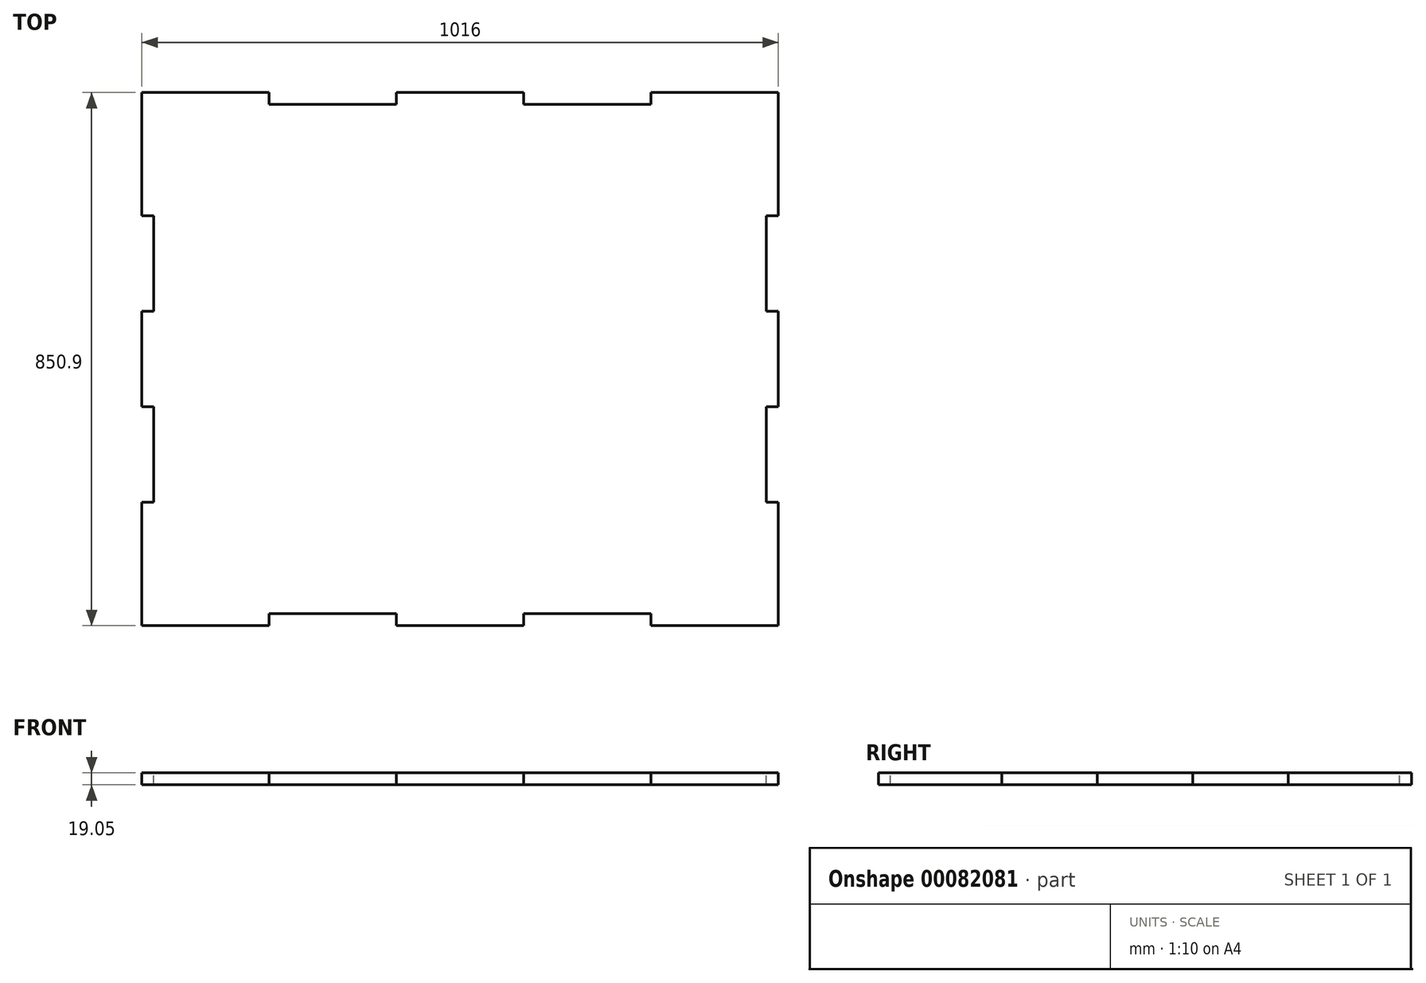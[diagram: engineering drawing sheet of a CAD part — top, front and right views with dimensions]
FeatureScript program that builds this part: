
annotation { "Feature Type Name" : "Feature", "Feature Type Description" : "" }
export const myFeature = defineFeature(function(context is Context, id is Id, definition is map)
    precondition{}
    {
        {
            var Q0;
            Q0=qCreatedBy(makeId("Top.planeOp"),FACE);
            var sketch = newSketch(context, id + "F0", { "sketchPlane" : qUnion([Q0])});
            skLineSegment(sketch, "E0.bottom", {"start": v(-612.36, 0) * mm, "end": v(403.64, 0) * mm});
            skLineSegment(sketch, "E0.top", {"start": v(-612.36, 838.2) * mm, "end": v(403.64, 838.2) * mm});
            skLineSegment(sketch, "E0.left", {"start": v(-612.36, 0) * mm, "end": v(-612.36, 838.2) * mm});
            skLineSegment(sketch, "E0.right", {"start": v(403.64, 0) * mm, "end": v(403.64, 838.2) * mm});
            skSolve(sketch);
        }
        {
            var Q0;
            Q0 = qSketchRegion(id + "F0", true);
            extrude(context, id + "F1", {"entities" : qUnion([Q0]), "depth" : 19.05 * mm});
        }
        {
            var Q0;
            Q0=makeQuery(id+"F1.opExtrude","CAP_FACE",FACE,{"disambiguationData":[OSD([sQuery(id+"F0.wireOp",EDGE,"E0.bottom"),sQuery(id+"F0.wireOp",EDGE,"E0.top"),sQuery(id+"F0.wireOp",EDGE,"E0.left"),sQuery(id+"F0.wireOp",EDGE,"E0.right")])],"isStart":false});
            var sketch = newSketch(context, id + "F2", { "sketchPlane" : qUnion([Q0])});
            skLineSegment(sketch, "E1", {"start": v(403.64, 190.5) * mm, "end": v(390.94, 190.5) * mm});
            skLineSegment(sketch, "E2", {"start": v(390.94, 190.5) * mm, "end": v(390.94, 342.9) * mm});
            skLineSegment(sketch, "E3", {"start": v(390.94, 342.9) * mm, "end": v(403.64, 342.9) * mm});
            skLineSegment(sketch, "E4", {"start": v(403.64, 495.3) * mm, "end": v(384.6, 495.3) * mm});
            skLineSegment(sketch, "E5", {"start": v(384.6, 495.3) * mm, "end": v(384.6, 647.7) * mm});
            skLineSegment(sketch, "E6", {"start": v(384.6, 647.7) * mm, "end": v(403.64, 647.7) * mm});
            skLineSegment(sketch, "E7.top", {"start": v(384.6, 495.3) * mm, "end": v(403.64, 495.3) * mm});
            skLineSegment(sketch, "E7.left", {"start": v(384.6, 647.7) * mm, "end": v(384.6, 495.3) * mm});
            skLineSegment(sketch, "E7.right", {"start": v(403.64, 647.7) * mm, "end": v(403.64, 495.3) * mm});
            skLineSegment(sketch, "E8.top", {"start": v(390.94, 190.5) * mm, "end": v(403.64, 190.5) * mm});
            skLineSegment(sketch, "E8.left", {"start": v(390.94, 342.9) * mm, "end": v(390.94, 190.5) * mm});
            skLineSegment(sketch, "E8.right", {"start": v(403.64, 342.9) * mm, "end": v(403.64, 190.5) * mm});
            skLineSegment(sketch, "E9.MirrorCS", {"start": v(-599.66, 342.9) * mm, "end": v(-612.36, 342.9) * mm});
            skLineSegment(sketch, "E10.MirrorCS", {"start": v(-599.66, 190.5) * mm, "end": v(-612.36, 190.5) * mm});
            skLineSegment(sketch, "E11.MirrorCS", {"start": v(-612.36, 190.5) * mm, "end": v(-599.66, 190.5) * mm});
            skLineSegment(sketch, "E12.MirrorCS", {"start": v(-599.66, 342.9) * mm, "end": v(-599.66, 190.5) * mm});
            skLineSegment(sketch, "E13.MirrorCS", {"start": v(-599.66, 190.5) * mm, "end": v(-599.66, 342.9) * mm});
            skLineSegment(sketch, "E14.MirrorCS", {"start": v(-612.36, 342.9) * mm, "end": v(-612.36, 190.5) * mm});
            skLineSegment(sketch, "E15.MirrorCS", {"start": v(-612.36, 495.3) * mm, "end": v(-599.66, 495.3) * mm});
            skLineSegment(sketch, "E16.MirrorCS", {"start": v(-599.66, 647.7) * mm, "end": v(-612.36, 647.7) * mm});
            skLineSegment(sketch, "E17.MirrorCS", {"start": v(-599.66, 495.3) * mm, "end": v(-612.36, 495.3) * mm});
            skLineSegment(sketch, "E18.MirrorCS", {"start": v(-599.66, 495.3) * mm, "end": v(-599.66, 647.7) * mm});
            skLineSegment(sketch, "E19.MirrorCS", {"start": v(-612.36, 647.7) * mm, "end": v(-612.36, 495.3) * mm});
            skLineSegment(sketch, "E20.MirrorCS", {"start": v(-599.66, 647.7) * mm, "end": v(-599.66, 495.3) * mm});
            skLineSegment(sketch, "E21", {"start": v(-409.16, 0) * mm, "end": v(-409.16, 19.05) * mm});
            skLineSegment(sketch, "E22", {"start": v(-409.16, 19.05) * mm, "end": v(-205.96, 19.05) * mm});
            skLineSegment(sketch, "E23", {"start": v(-205.96, 19.05) * mm, "end": v(-205.96, 0) * mm});
            skLineSegment(sketch, "E24", {"start": v(-2.76, 0) * mm, "end": v(-2.76, 19.05) * mm});
            skLineSegment(sketch, "E25", {"start": v(-2.76, 19.05) * mm, "end": v(200.44, 19.05) * mm});
            skLineSegment(sketch, "E26", {"start": v(200.44, 19.05) * mm, "end": v(200.44, 0) * mm});
            skLineSegment(sketch, "E27", {"start": v(-409.16, 0) * mm, "end": v(-205.96, 0) * mm});
            skLineSegment(sketch, "E28", {"start": v(403.64, 419.1) * mm, "end": v(-612.36, 419.1) * mm});
            skLineSegment(sketch, "E29.MirrorCS", {"start": v(200.44, 819.15) * mm, "end": v(200.44, 838.2) * mm});
            skLineSegment(sketch, "E30.MirrorCS", {"start": v(-409.16, 838.2) * mm, "end": v(-409.16, 819.15) * mm});
            skLineSegment(sketch, "E31.MirrorCS", {"start": v(-205.96, 819.15) * mm, "end": v(-205.96, 838.2) * mm});
            skLineSegment(sketch, "E32.MirrorCS", {"start": v(-2.76, 819.15) * mm, "end": v(200.44, 819.15) * mm});
            skLineSegment(sketch, "E33.MirrorCS", {"start": v(-409.16, 838.2) * mm, "end": v(-205.96, 838.2) * mm});
            skLineSegment(sketch, "E34.MirrorCS", {"start": v(-2.76, 838.2) * mm, "end": v(-2.76, 819.15) * mm});
            skLineSegment(sketch, "E35.MirrorCS", {"start": v(-409.16, 819.15) * mm, "end": v(-205.96, 819.15) * mm});
            skLineSegment(sketch, "E36", {"start": v(-2.76, 838.2) * mm, "end": v(200.44, 838.2) * mm});
            skLineSegment(sketch, "E37", {"start": v(-2.76, 0) * mm, "end": v(200.44, 0) * mm});
            skSolve(sketch);
        }
        {
            var Q0;
            Q0 = qSketchRegion(id + "F2", true);
            extrude(context, id + "F3", {"entities" : qUnion([Q0]), "operationType" : NewBodyOperationType.REMOVE, "endBound" : BoundingType.THROUGH_ALL, "oppositeDirection" : true, "depth" : 25.4 * mm});
        }
        {
            var Q0;
            Q0=makeQuery(id+"F1.opExtrude","CAP_FACE",FACE,{"disambiguationData":[OSD([sQuery(id+"F0.wireOp",EDGE,"E0.bottom"),sQuery(id+"F0.wireOp",EDGE,"E0.top"),sQuery(id+"F0.wireOp",EDGE,"E0.left"),sQuery(id+"F0.wireOp",EDGE,"E0.right")])],"isStart":false});
            var sketch = newSketch(context, id + "F4", { "sketchPlane" : qUnion([Q0])});
            skLineSegment(sketch, "E38.0", {"start": v(-612.36, 844.55) * mm, "end": v(-409.16, 844.55) * mm});
            skLineSegment(sketch, "E39.0", {"start": v(200.44, 825.5) * mm, "end": v(-2.76, 825.5) * mm});
            skLineSegment(sketch, "E40.top", {"start": v(-612.36, 838.2) * mm, "end": v(-409.16, 838.2) * mm});
            skLineSegment(sketch, "E40.left", {"start": v(-612.36, 844.55) * mm, "end": v(-612.36, 838.2) * mm});
            skLineSegment(sketch, "E40.right", {"start": v(-409.16, 844.55) * mm, "end": v(-409.16, 838.2) * mm});
            skLineSegment(sketch, "E41.bottom", {"start": v(-409.16, 825.5) * mm, "end": v(-205.96, 825.5) * mm});
            skLineSegment(sketch, "E41.top", {"start": v(-409.16, 819.15) * mm, "end": v(-205.96, 819.15) * mm});
            skLineSegment(sketch, "E41.left", {"start": v(-409.16, 825.5) * mm, "end": v(-409.16, 819.15) * mm});
            skLineSegment(sketch, "E41.right", {"start": v(-205.96, 825.5) * mm, "end": v(-205.96, 819.15) * mm});
            skLineSegment(sketch, "E42.bottom", {"start": v(-205.96, 838.2) * mm, "end": v(-2.76, 838.2) * mm});
            skLineSegment(sketch, "E42.top", {"start": v(-205.96, 844.55) * mm, "end": v(-2.76, 844.55) * mm});
            skLineSegment(sketch, "E42.left", {"start": v(-205.96, 838.2) * mm, "end": v(-205.96, 844.55) * mm});
            skLineSegment(sketch, "E42.right", {"start": v(-2.76, 838.2) * mm, "end": v(-2.76, 844.55) * mm});
            skLineSegment(sketch, "E43.bottom", {"start": v(-2.76, 819.15) * mm, "end": v(200.44, 819.15) * mm});
            skLineSegment(sketch, "E43.top", {"start": v(-2.76, 825.5) * mm, "end": v(200.44, 825.5) * mm});
            skLineSegment(sketch, "E43.left", {"start": v(-2.76, 819.15) * mm, "end": v(-2.76, 825.5) * mm});
            skLineSegment(sketch, "E43.right", {"start": v(200.44, 819.15) * mm, "end": v(200.44, 825.5) * mm});
            skLineSegment(sketch, "E44.bottom", {"start": v(403.64, 844.55) * mm, "end": v(200.44, 844.55) * mm});
            skLineSegment(sketch, "E44.top", {"start": v(403.64, 838.2) * mm, "end": v(200.44, 838.2) * mm});
            skLineSegment(sketch, "E44.left", {"start": v(403.64, 844.55) * mm, "end": v(403.64, 838.2) * mm});
            skLineSegment(sketch, "E44.right", {"start": v(200.44, 844.55) * mm, "end": v(200.44, 838.2) * mm});
            skLineSegment(sketch, "E45.trimOffspring", {"start": v(200.44, 844.55) * mm, "end": v(403.64, 844.55) * mm});
            skLineSegment(sketch, "E46.trimOffspring", {"start": v(-205.96, 825.5) * mm, "end": v(-409.16, 825.5) * mm});
            skLineSegment(sketch, "E47", {"start": v(-409.16, 19.05) * mm, "end": v(-205.96, 19.05) * mm});
            skLineSegment(sketch, "E48", {"start": v(-612.36, 0) * mm, "end": v(-409.16, 0) * mm});
            skLineSegment(sketch, "E49.0", {"start": v(-612.36, -6.35) * mm, "end": v(-409.16, -6.35) * mm});
            skLineSegment(sketch, "E50.0", {"start": v(-409.16, 12.7) * mm, "end": v(-205.96, 12.7) * mm});
            skLineSegment(sketch, "E51.left", {"start": v(-409.16, 12.7) * mm, "end": v(-409.16, 19.05) * mm});
            skLineSegment(sketch, "E51.right", {"start": v(-205.96, 12.7) * mm, "end": v(-205.96, 19.05) * mm});
            skLineSegment(sketch, "E52.bottom", {"start": v(200.44, 12.7) * mm, "end": v(-2.76, 12.7) * mm});
            skLineSegment(sketch, "E52.top", {"start": v(200.44, 19.05) * mm, "end": v(-2.76, 19.05) * mm});
            skLineSegment(sketch, "E52.left", {"start": v(200.44, 12.7) * mm, "end": v(200.44, 19.05) * mm});
            skLineSegment(sketch, "E52.right", {"start": v(-2.76, 12.7) * mm, "end": v(-2.76, 19.05) * mm});
            skLineSegment(sketch, "E53.bottom", {"start": v(200.44, 0) * mm, "end": v(403.64, 0) * mm});
            skLineSegment(sketch, "E53.top", {"start": v(200.44, -6.35) * mm, "end": v(403.64, -6.35) * mm});
            skLineSegment(sketch, "E53.left", {"start": v(200.44, 0) * mm, "end": v(200.44, -6.35) * mm});
            skLineSegment(sketch, "E53.right", {"start": v(403.64, 0) * mm, "end": v(403.64, -6.35) * mm});
            skLineSegment(sketch, "E54.bottom", {"start": v(-205.96, 0) * mm, "end": v(-2.76, 0) * mm});
            skLineSegment(sketch, "E54.top", {"start": v(-205.96, -6.35) * mm, "end": v(-2.76, -6.35) * mm});
            skLineSegment(sketch, "E54.left", {"start": v(-205.96, 0) * mm, "end": v(-205.96, -6.35) * mm});
            skLineSegment(sketch, "E54.right", {"start": v(-2.76, 0) * mm, "end": v(-2.76, -6.35) * mm});
            skLineSegment(sketch, "E55.left", {"start": v(-612.36, 0) * mm, "end": v(-612.36, -6.35) * mm});
            skLineSegment(sketch, "E55.right", {"start": v(-409.16, 0) * mm, "end": v(-409.16, -6.35) * mm});
            skLineSegment(sketch, "E56.trimOffspring", {"start": v(-2.76, 12.7) * mm, "end": v(200.44, 12.7) * mm});
            skLineSegment(sketch, "E57.trimOffspring", {"start": v(-2.76, 19.05) * mm, "end": v(200.44, 19.05) * mm});
            skLineSegment(sketch, "E58.left", {"start": v(-599.66, 342.9) * mm, "end": v(-599.66, 190.5) * mm});
            skLineSegment(sketch, "E59.bottom", {"start": v(-599.66, 647.7) * mm, "end": v(-593.3, 647.7) * mm});
            skLineSegment(sketch, "E59.top", {"start": v(-599.66, 495.3) * mm, "end": v(-593.3, 495.3) * mm});
            skLineSegment(sketch, "E59.left", {"start": v(-599.66, 647.7) * mm, "end": v(-599.66, 495.3) * mm});
            skLineSegment(sketch, "E59.right", {"start": v(-593.3, 647.7) * mm, "end": v(-593.3, 495.3) * mm});
            skLineSegment(sketch, "E60.bottom", {"start": v(-599.66, 342.9) * mm, "end": v(-593.3, 342.9) * mm});
            skLineSegment(sketch, "E60.top", {"start": v(-599.66, 190.5) * mm, "end": v(-593.3, 190.5) * mm});
            skLineSegment(sketch, "E60.right", {"start": v(-593.3, 342.9) * mm, "end": v(-593.3, 190.5) * mm});
            skLineSegment(sketch, "E61.bottom", {"start": v(390.94, 342.9) * mm, "end": v(384.6, 342.9) * mm});
            skLineSegment(sketch, "E61.top", {"start": v(390.94, 190.5) * mm, "end": v(384.6, 190.5) * mm});
            skLineSegment(sketch, "E61.left", {"start": v(390.94, 342.9) * mm, "end": v(390.94, 190.5) * mm});
            skLineSegment(sketch, "E61.right", {"start": v(384.6, 342.9) * mm, "end": v(384.6, 190.5) * mm});
            skLineSegment(sketch, "E62.bottom", {"start": v(384.6, 647.7) * mm, "end": v(378.24, 647.7) * mm});
            skLineSegment(sketch, "E62.top", {"start": v(384.6, 495.3) * mm, "end": v(378.24, 495.3) * mm});
            skLineSegment(sketch, "E62.left", {"start": v(384.6, 647.7) * mm, "end": v(384.6, 495.3) * mm});
            skLineSegment(sketch, "E62.right", {"start": v(378.24, 647.7) * mm, "end": v(378.24, 495.3) * mm});
            skSolve(sketch);
        }
        {
            var Q0;
            Q0 = qSketchRegion(id + "F4", true);
            extrude(context, id + "F5", {"entities" : qUnion([Q0]), "operationType" : NewBodyOperationType.ADD, "oppositeDirection" : true, "depth" : 19.05 * mm});
        }
        {
            var Q0;
            Q0=makeQuery(id+"F5.boolean.opBoolean","MERGE",FACE,{"derivedFrom":[makeQuery(id+"F1.opExtrude","CAP_FACE",FACE,{"disambiguationData":[OSD([sQuery(id+"F0.wireOp",EDGE,"E0.bottom"),sQuery(id+"F0.wireOp",EDGE,"E0.top"),sQuery(id+"F0.wireOp",EDGE,"E0.left"),sQuery(id+"F0.wireOp",EDGE,"E0.right")])],"isStart":false}),makeQuery(id+"F5.opExtrude","CAP_FACE",FACE,{"disambiguationData":[OSD([sQuery(id+"F4.wireOp",EDGE,"E38.0"),sQuery(id+"F4.wireOp",EDGE,"E40.top"),sQuery(id+"F4.wireOp",EDGE,"E40.left"),sQuery(id+"F4.wireOp",EDGE,"E40.right")])],"isStart":true}),makeQuery(id+"F5.opExtrude","CAP_FACE",FACE,{"disambiguationData":[OSD([sQuery(id+"F4.wireOp",EDGE,"E41.top"),sQuery(id+"F4.wireOp",EDGE,"E41.left"),sQuery(id+"F4.wireOp",EDGE,"E41.right"),sQuery(id+"F4.wireOp",EDGE,"E46.trimOffspring")])],"isStart":true}),makeQuery(id+"F5.opExtrude","CAP_FACE",FACE,{"disambiguationData":[OSD([sQuery(id+"F4.wireOp",EDGE,"E42.bottom"),sQuery(id+"F4.wireOp",EDGE,"E42.left"),sQuery(id+"F4.wireOp",EDGE,"E42.right"),sQuery(id+"F4.wireOp",EDGE,"E42.top")])],"isStart":true}),makeQuery(id+"F5.opExtrude","CAP_FACE",FACE,{"disambiguationData":[OSD([sQuery(id+"F4.wireOp",EDGE,"E43.bottom"),sQuery(id+"F4.wireOp",EDGE,"E43.top"),sQuery(id+"F4.wireOp",EDGE,"E43.left"),sQuery(id+"F4.wireOp",EDGE,"E43.right")])],"isStart":true}),makeQuery(id+"F5.opExtrude","CAP_FACE",FACE,{"disambiguationData":[OSD([sQuery(id+"F4.wireOp",EDGE,"E44.top"),sQuery(id+"F4.wireOp",EDGE,"E44.left"),sQuery(id+"F4.wireOp",EDGE,"E44.right"),sQuery(id+"F4.wireOp",EDGE,"E45.trimOffspring")])],"isStart":true}),makeQuery(id+"F5.opExtrude","CAP_FACE",FACE,{"disambiguationData":[OSD([sQuery(id+"F4.wireOp",EDGE,"E50.0"),sQuery(id+"F4.wireOp",EDGE,"E47"),sQuery(id+"F4.wireOp",EDGE,"E51.left"),sQuery(id+"F4.wireOp",EDGE,"E51.right")])],"isStart":true}),makeQuery(id+"F5.opExtrude","CAP_FACE",FACE,{"disambiguationData":[OSD([sQuery(id+"F4.wireOp",EDGE,"E52.left"),sQuery(id+"F4.wireOp",EDGE,"E52.right"),sQuery(id+"F4.wireOp",EDGE,"E56.trimOffspring"),sQuery(id+"F4.wireOp",EDGE,"E57.trimOffspring")])],"isStart":true}),makeQuery(id+"F5.opExtrude","CAP_FACE",FACE,{"disambiguationData":[OSD([sQuery(id+"F4.wireOp",EDGE,"E53.left"),sQuery(id+"F4.wireOp",EDGE,"E53.right"),sQuery(id+"F4.wireOp",EDGE,"E53.bottom"),sQuery(id+"F4.wireOp",EDGE,"E53.top")])],"isStart":true}),makeQuery(id+"F5.opExtrude","CAP_FACE",FACE,{"disambiguationData":[OSD([sQuery(id+"F4.wireOp",EDGE,"E54.left"),sQuery(id+"F4.wireOp",EDGE,"E54.right"),sQuery(id+"F4.wireOp",EDGE,"E54.top"),sQuery(id+"F4.wireOp",EDGE,"E54.bottom")])],"isStart":true}),makeQuery(id+"F5.opExtrude","CAP_FACE",FACE,{"disambiguationData":[OSD([sQuery(id+"F4.wireOp",EDGE,"E48"),sQuery(id+"F4.wireOp",EDGE,"E49.0"),sQuery(id+"F4.wireOp",EDGE,"E55.left"),sQuery(id+"F4.wireOp",EDGE,"E55.right")])],"isStart":true})]});
            var sketch = newSketch(context, id + "F6", { "sketchPlane" : qUnion([Q0])});
            skLineSegment(sketch, "E63.bottom", {"start": v(-599.66, 647.7) * mm, "end": v(-593.3, 647.7) * mm});
            skLineSegment(sketch, "E63.top", {"start": v(-599.66, 495.3) * mm, "end": v(-593.3, 495.3) * mm});
            skLineSegment(sketch, "E63.left", {"start": v(-599.66, 647.7) * mm, "end": v(-599.66, 495.3) * mm});
            skLineSegment(sketch, "E63.right", {"start": v(-593.3, 647.7) * mm, "end": v(-593.3, 495.3) * mm});
            skLineSegment(sketch, "E64.bottom", {"start": v(-599.66, 342.9) * mm, "end": v(-593.3, 342.9) * mm});
            skLineSegment(sketch, "E64.top", {"start": v(-599.66, 190.5) * mm, "end": v(-593.3, 190.5) * mm});
            skLineSegment(sketch, "E64.left", {"start": v(-599.66, 342.9) * mm, "end": v(-599.66, 190.5) * mm});
            skLineSegment(sketch, "E64.right", {"start": v(-593.3, 342.9) * mm, "end": v(-593.3, 190.5) * mm});
            skLineSegment(sketch, "E65", {"start": v(-104.36, 844.55) * mm, "end": v(-104.36, 682.26) * mm});
            skLineSegment(sketch, "E66.MirrorCS", {"start": v(390.94, 190.5) * mm, "end": v(384.6, 190.5) * mm});
            skLineSegment(sketch, "E67.MirrorCS", {"start": v(390.94, 342.9) * mm, "end": v(384.6, 342.9) * mm});
            skLineSegment(sketch, "E68.MirrorCS", {"start": v(390.94, 495.3) * mm, "end": v(384.6, 495.3) * mm});
            skLineSegment(sketch, "E69.MirrorCS", {"start": v(390.94, 647.7) * mm, "end": v(384.6, 647.7) * mm});
            skLineSegment(sketch, "E70.MirrorCS", {"start": v(384.6, 342.9) * mm, "end": v(384.6, 190.5) * mm});
            skLineSegment(sketch, "E71.MirrorCS", {"start": v(390.94, 342.9) * mm, "end": v(390.94, 190.5) * mm});
            skLineSegment(sketch, "E72.MirrorCS", {"start": v(384.6, 647.7) * mm, "end": v(384.6, 495.3) * mm});
            skLineSegment(sketch, "E73.MirrorCS", {"start": v(390.94, 647.7) * mm, "end": v(390.94, 495.3) * mm});
            skSolve(sketch);
        }
        {
            var Q0;
            Q0 = qSketchRegion(id + "F6", true);
            extrude(context, id + "F7", {"entities" : qUnion([Q0]), "operationType" : NewBodyOperationType.REMOVE, "endBound" : BoundingType.THROUGH_ALL, "oppositeDirection" : true, "depth" : 25.4 * mm});
        }
    });
